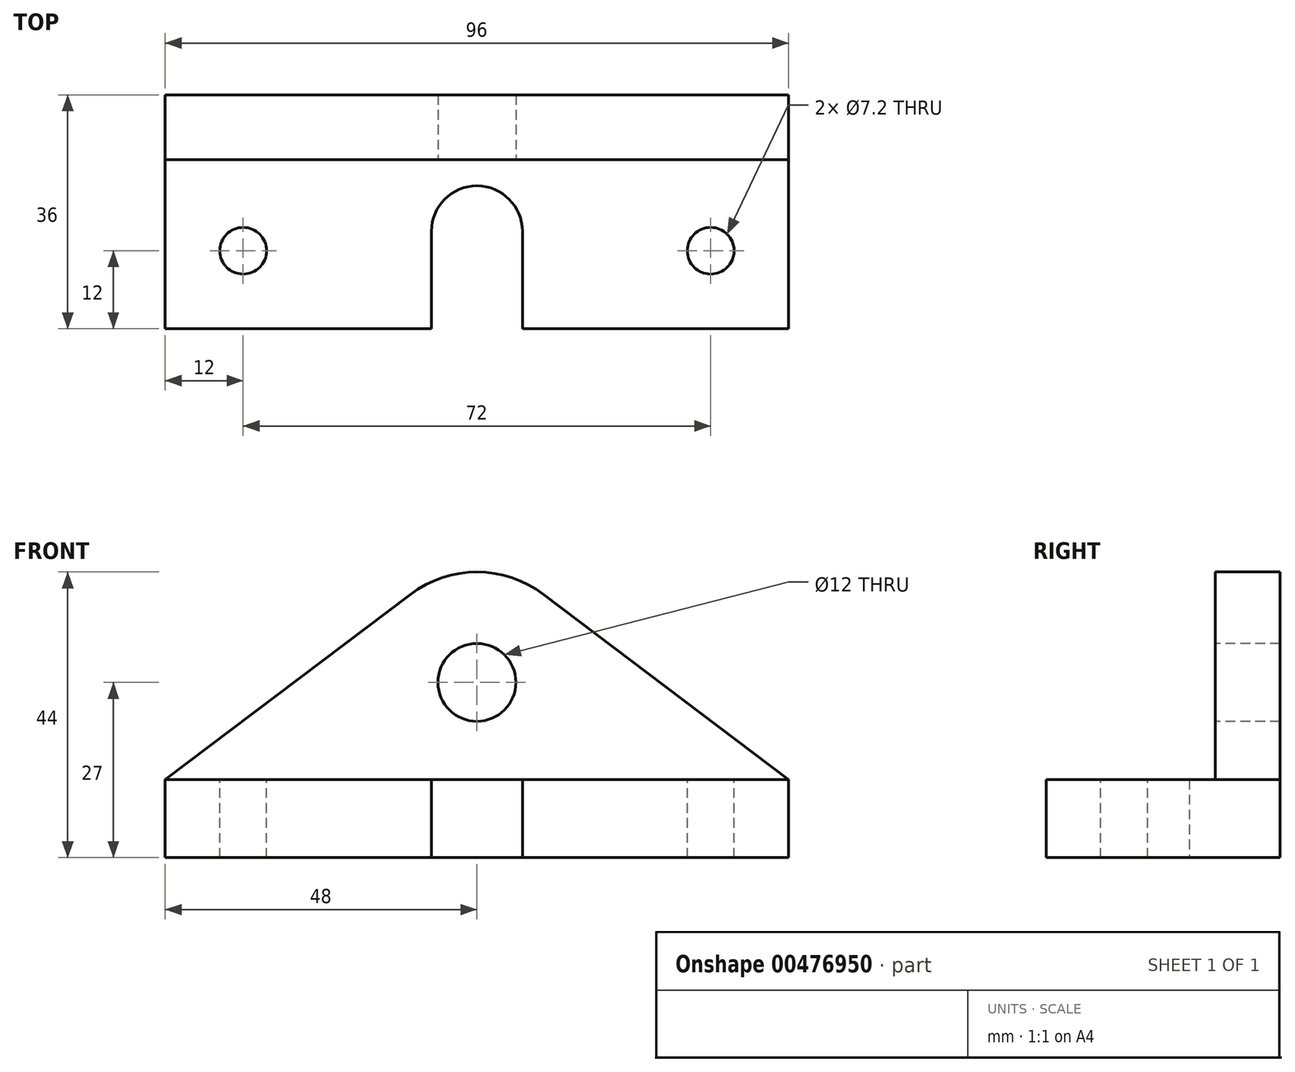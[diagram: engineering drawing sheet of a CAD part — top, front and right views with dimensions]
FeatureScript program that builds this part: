
annotation { "Feature Type Name" : "Feature", "Feature Type Description" : "" }
export const myFeature = defineFeature(function(context is Context, id is Id, definition is map)
    precondition{}
    {
        {
            var Q0;
            Q0=qCreatedBy(makeId("Top.planeOp"),FACE);
            var sketch = newSketch(context, id + "F0", { "sketchPlane" : qUnion([Q0])});
            skLineSegment(sketch, "E0.bottom", {"start": v(48, -18) * mm, "end": v(7, -18) * mm});
            skLineSegment(sketch, "E0.top", {"start": v(48, 18) * mm, "end": v(-48, 18) * mm});
            skLineSegment(sketch, "E0.left", {"start": v(48, -18) * mm, "end": v(48, 18) * mm});
            skLineSegment(sketch, "E0.right", {"start": v(-48, -18) * mm, "end": v(-48, 18) * mm});
            skPoint(sketch, "E0.middle", {"position": v(0, 0) * mm});
            skArc(sketch, "E1", {"start": v(7, -3) * mm, "mid": v(0, 4) * mm, "end": v(-7, -3) * mm});
            skLineSegment(sketch, "E2", {"start": v(-7, -18) * mm, "end": v(-7, -3) * mm});
            skArc(sketch, "E3.MirrorC", {"start": v(-7, -3) * mm, "mid": v(0, 4) * mm, "end": v(7, -3) * mm});
            skLineSegment(sketch, "E4.MirrorCS", {"start": v(7, -18) * mm, "end": v(7, -3) * mm});
            skLineSegment(sketch, "E5.trimOffspring", {"start": v(-7, -18) * mm, "end": v(-48, -18) * mm});
            skSolve(sketch);
        }
        {
            var Q0;
            Q0 = qSketchRegion(id + "F0", true);
            extrude(context, id + "F1", {"entities" : qUnion([Q0]), "depth" : 12 * mm});
        }
        {
            var Q0;
            Q0=makeQuery(id+"F1.opExtrude","CAP_FACE",FACE,{"disambiguationData":[OSD([sQuery(id+"F0.wireOp",EDGE,"E0.bottom"),sQuery(id+"F0.wireOp",EDGE,"E0.top"),sQuery(id+"F0.wireOp",EDGE,"E0.left"),sQuery(id+"F0.wireOp",EDGE,"E0.right"),sQuery(id+"F0.wireOp",EDGE,"E2"),sQuery(id+"F0.wireOp",EDGE,"E1"),sQuery(id+"F0.wireOp",EDGE,"E4.MirrorCS"),sQuery(id+"F0.wireOp",EDGE,"E5.trimOffspring")])],"isStart":false});
            var sketch = newSketch(context, id + "F2", { "sketchPlane" : qUnion([Q0])});
            skLineSegment(sketch, "E6", {"start": v(0, -31.83) * mm, "end": v(0, 27.88) * mm, "construction": true});
            skPoint(sketch, "E6.endSnap0", {"position": v(0, 18) * mm});
            skLineSegment(sketch, "E7", {"start": v(48, -18) * mm, "end": v(48, -6) * mm, "construction": true});
            skLineSegment(sketch, "E8", {"start": v(0, -6) * mm, "end": v(36, -6) * mm, "construction": true});
            skCircle(sketch, "E9", {"center": v(36, -6) * mm, "radius": 3.6 * mm});
            skCircle(sketch, "E10.MirrorC", {"center": v(-36, -6) * mm, "radius": 3.6 * mm});
            skSolve(sketch);
        }
        {
            var Q0;
            Q0 = qSketchRegion(id + "F2", true);
            extrude(context, id + "F3", {"entities" : qUnion([Q0]), "operationType" : NewBodyOperationType.REMOVE, "endBound" : BoundingType.THROUGH_ALL, "oppositeDirection" : true, "depth" : 25 * mm});
        }
        {
            var Q0;
            Q0=makeQuery(id+"F1.opExtrude","CAP_FACE",FACE,{"disambiguationData":[OSD([sQuery(id+"F0.wireOp",EDGE,"E0.bottom"),sQuery(id+"F0.wireOp",EDGE,"E0.top"),sQuery(id+"F0.wireOp",EDGE,"E0.left"),sQuery(id+"F0.wireOp",EDGE,"E0.right"),sQuery(id+"F0.wireOp",EDGE,"E2"),sQuery(id+"F0.wireOp",EDGE,"E1"),sQuery(id+"F0.wireOp",EDGE,"E4.MirrorCS"),sQuery(id+"F0.wireOp",EDGE,"E5.trimOffspring")])],"isStart":false});
            var sketch = newSketch(context, id + "F4", { "sketchPlane" : qUnion([Q0])});
            skLineSegment(sketch, "E11", {"start": v(-48, 18) * mm, "end": v(-48, 8) * mm});
            skLineSegment(sketch, "E12", {"start": v(-48, 8) * mm, "end": v(48, 8) * mm});
            skLineSegment(sketch, "E13", {"start": v(48, 8) * mm, "end": v(48, 18) * mm});
            skLineSegment(sketch, "E14", {"start": v(48, 18) * mm, "end": v(-48, 18) * mm});
            skSolve(sketch);
        }
        {
            var Q0;
            Q0 = qSketchRegion(id + "F4", true);
            extrude(context, id + "F5", {"entities" : qUnion([Q0]), "operationType" : NewBodyOperationType.ADD, "depth" : 32 * mm});
        }
        {
            var Q0;
            Q0=makeQuery(id+"F5.opExtrude","SWEPT_FACE",FACE,{"disambiguationData":[OSD([sQuery(id+"F4.wireOp",EDGE,"E12")])]});
            var sketch = newSketch(context, id + "F6", { "sketchPlane" : qUnion([Q0])});
            skLineSegment(sketch, "E15", {"start": v(0, 12) * mm, "end": v(0, 27) * mm, "construction": true});
            skPoint(sketch, "E15.endSnap0", {"position": v(0, 44) * mm});
            skCircle(sketch, "E16", {"center": v(0, 27) * mm, "radius": 6 * mm});
            skSolve(sketch);
        }
        {
            var Q0;
            Q0 = qSketchRegion(id + "F6", true);
            extrude(context, id + "F7", {"entities" : qUnion([Q0]), "operationType" : NewBodyOperationType.REMOVE, "endBound" : BoundingType.THROUGH_ALL, "oppositeDirection" : true, "depth" : 10 * mm});
        }
        {
            var Q0;
            Q0=makeQuery(id+"F5.opExtrude","SWEPT_FACE",FACE,{"disambiguationData":[OSD([sQuery(id+"F4.wireOp",EDGE,"E12")])]});
            var sketch = newSketch(context, id + "F8", { "sketchPlane" : qUnion([Q0])});
            skArc(sketch, "E17", {"start": v(10.26, 40.56) * mm, "mid": v(0, 44) * mm, "end": v(-10.26, 40.56) * mm});
            skLineSegment(sketch, "E18", {"start": v(-48, 12) * mm, "end": v(-10.26, 40.56) * mm});
            skLineSegment(sketch, "E19", {"start": v(0, 46.96) * mm, "end": v(0, 10) * mm, "construction": true});
            skPoint(sketch, "E19.startSnap0", {"position": v(0, 44) * mm});
            skLineSegment(sketch, "E20.MirrorCS", {"start": v(48, 12) * mm, "end": v(10.26, 40.56) * mm});
            skPoint(sketch, "E21.orphan", {"position": v(-5.7, 44) * mm});
            skPoint(sketch, "E22.orphan", {"position": v(5.7, 44) * mm});
            skLineSegment(sketch, "E23", {"start": v(-48, 12) * mm, "end": v(-48, 44.92) * mm});
            skLineSegment(sketch, "E24", {"start": v(-48, 44.92) * mm, "end": v(48, 44.92) * mm});
            skLineSegment(sketch, "E25", {"start": v(48, 44.92) * mm, "end": v(48, 12) * mm});
            skSolve(sketch);
        }
        {
            var Q0;
            {var subQ0=sQuery(id+"F8.wireOp",EDGE,"E20.MirrorCS");Q0=makeQuery(id+"F8.imprint","IMPRINT",FACE,{"disambiguationData":[TD([[makeQuery(id+"F8.imprint","IMPRINT",EDGE,{"derivedFrom":subQ0}),-1.0]])]});}
            var Q1;
            {var subQ0=sQuery(id+"F8.wireOp",EDGE,"E18");Q1=makeQuery(id+"F8.imprint","IMPRINT",FACE,{"disambiguationData":[TD([[makeQuery(id+"F8.imprint","IMPRINT",EDGE,{"derivedFrom":subQ0}),1.0]])]});}
            extrude(context, id + "F9", {"entities" : qUnion([Q0, Q1]), "operationType" : NewBodyOperationType.REMOVE, "oppositeDirection" : true, "depth" : 25 * mm});
        }
    });
